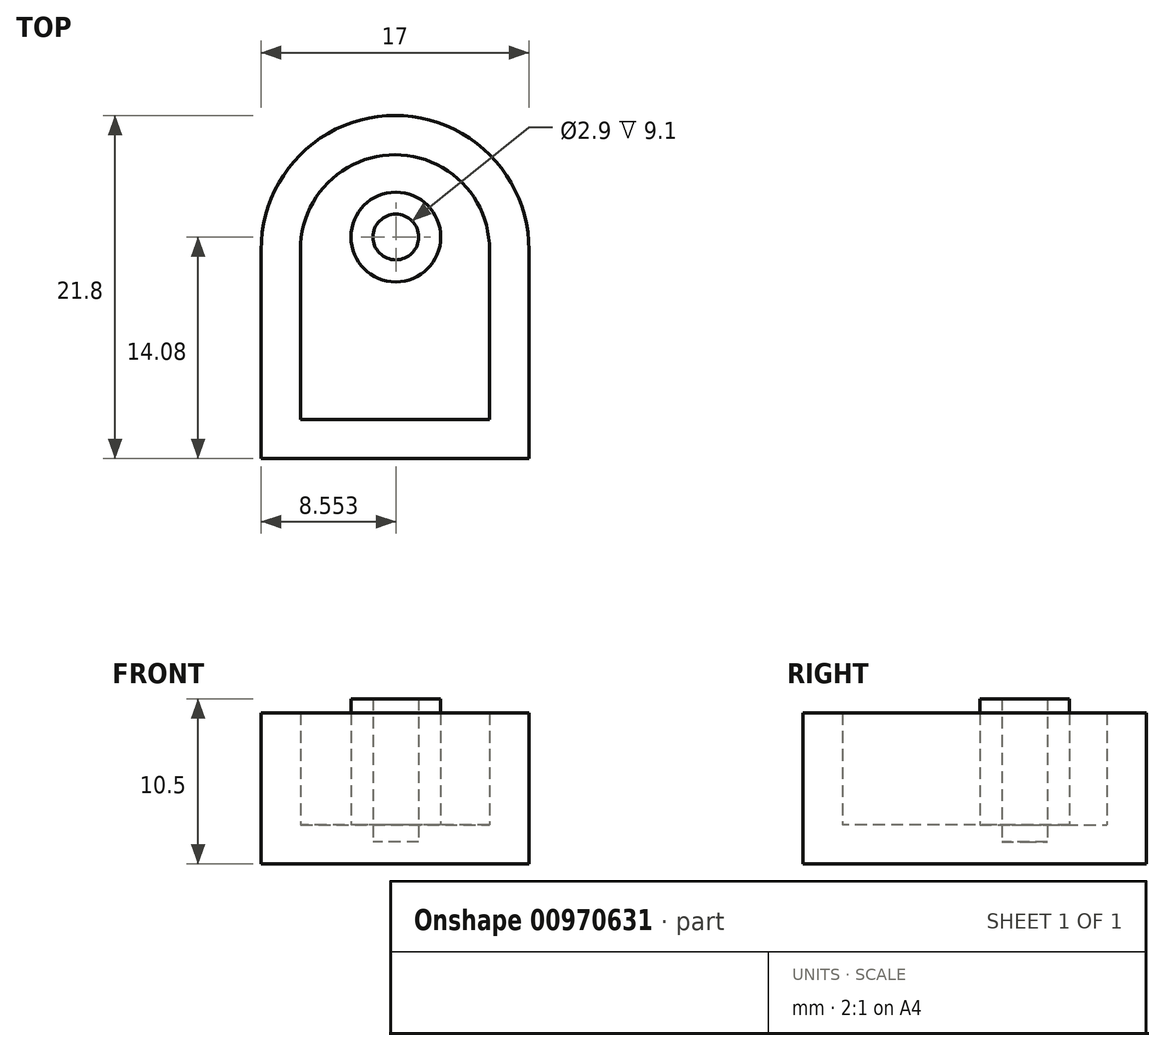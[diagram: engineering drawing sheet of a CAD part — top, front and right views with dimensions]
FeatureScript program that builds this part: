
annotation { "Feature Type Name" : "Feature", "Feature Type Description" : "" }
export const myFeature = defineFeature(function(context is Context, id is Id, definition is map)
    precondition{}
    {
        {
            var Q0;
            Q0=qCreatedBy(makeId("Top.planeOp"),FACE);
            var sketch = newSketch(context, id + "F0", { "sketchPlane" : qUnion([Q0])});
            skLineSegment(sketch, "E0.top", {"start": v(-7.8, -12.5) * mm, "end": v(9.2, -12.5) * mm});
            skLineSegment(sketch, "E0.left", {"start": v(-7.8, 0.75) * mm, "end": v(-7.8, -12.5) * mm});
            skLineSegment(sketch, "E0.right", {"start": v(9.2, 0.75) * mm, "end": v(9.2, -12.5) * mm});
            skArc(sketch, "E1", {"start": v(9.2, 0.75) * mm, "mid": v(0.7, 9.3) * mm, "end": v(-7.8, 0.75) * mm});
            skSolve(sketch);
        }
        {
            var Q0;
            Q0=makeQuery(id+"F0.imprint","IMPRINT",FACE,{"disambiguationData":[TD([[makeQuery(id+"F0.imprint","IMPRINT",EDGE,{"derivedFrom":sQuery(id+"F0.wireOp",EDGE,"E0.top")}),1.0]])]});
            extrude(context, id + "F1", {"entities" : qUnion([Q0]), "depth" : 9.6 * mm, "offsetDistance" : 25 * mm});
        }
        {
            var Q0;
            Q0=makeQuery(id+"F1.opExtrude","CAP_FACE",FACE,{"disambiguationData":[OSD([sQuery(id+"F0.wireOp",EDGE,"E0.top"),sQuery(id+"F0.wireOp",EDGE,"E0.left"),sQuery(id+"F0.wireOp",EDGE,"E0.right"),sQuery(id+"F0.wireOp",EDGE,"E1")])],"isStart":false});
            shell(context, id + "F2", {"entities" : qUnion([Q0]), "thickness" : 2.5 * mm});
        }
        {
            var Q0;
            Q0=makeQuery(id+"F2.opShell","OFFSET_FACE",FACE,{"disambiguationData":[OSD([sQuery(id+"F0.wireOp",EDGE,"E0.top"),sQuery(id+"F0.wireOp",EDGE,"E0.left"),sQuery(id+"F0.wireOp",EDGE,"E0.right"),sQuery(id+"F0.wireOp",EDGE,"E1")])]});
            var sketch = newSketch(context, id + "F3", { "sketchPlane" : qUnion([Q0])});
            skCircle(sketch, "E2", {"center": v(0.74, 1.58) * mm, "radius": 2.85 * mm});
            skSolve(sketch);
        }
        {
            var Q0;
            Q0=makeQuery(id+"F3.imprint","IMPRINT",FACE,{"disambiguationData":[TD([[makeQuery(id+"F3.imprint","IMPRINT",EDGE,{"derivedFrom":sQuery(id+"F3.wireOp",EDGE,"E2")}),1.0]])]});
            extrude(context, id + "F4", {"entities" : qUnion([Q0]), "operationType" : NewBodyOperationType.ADD, "depth" : 8 * mm, "offsetDistance" : 25 * mm});
        }
        {
            var Q0;
            Q0=makeQuery(id+"F4.opExtrude","CAP_FACE",FACE,{"disambiguationData":[OSD([sQuery(id+"F3.wireOp",EDGE,"E2")])],"isStart":false});
            shell(context, id + "F5", {"entities" : qUnion([Q0]), "thickness" : 1.4 * mm});
        }
    });
